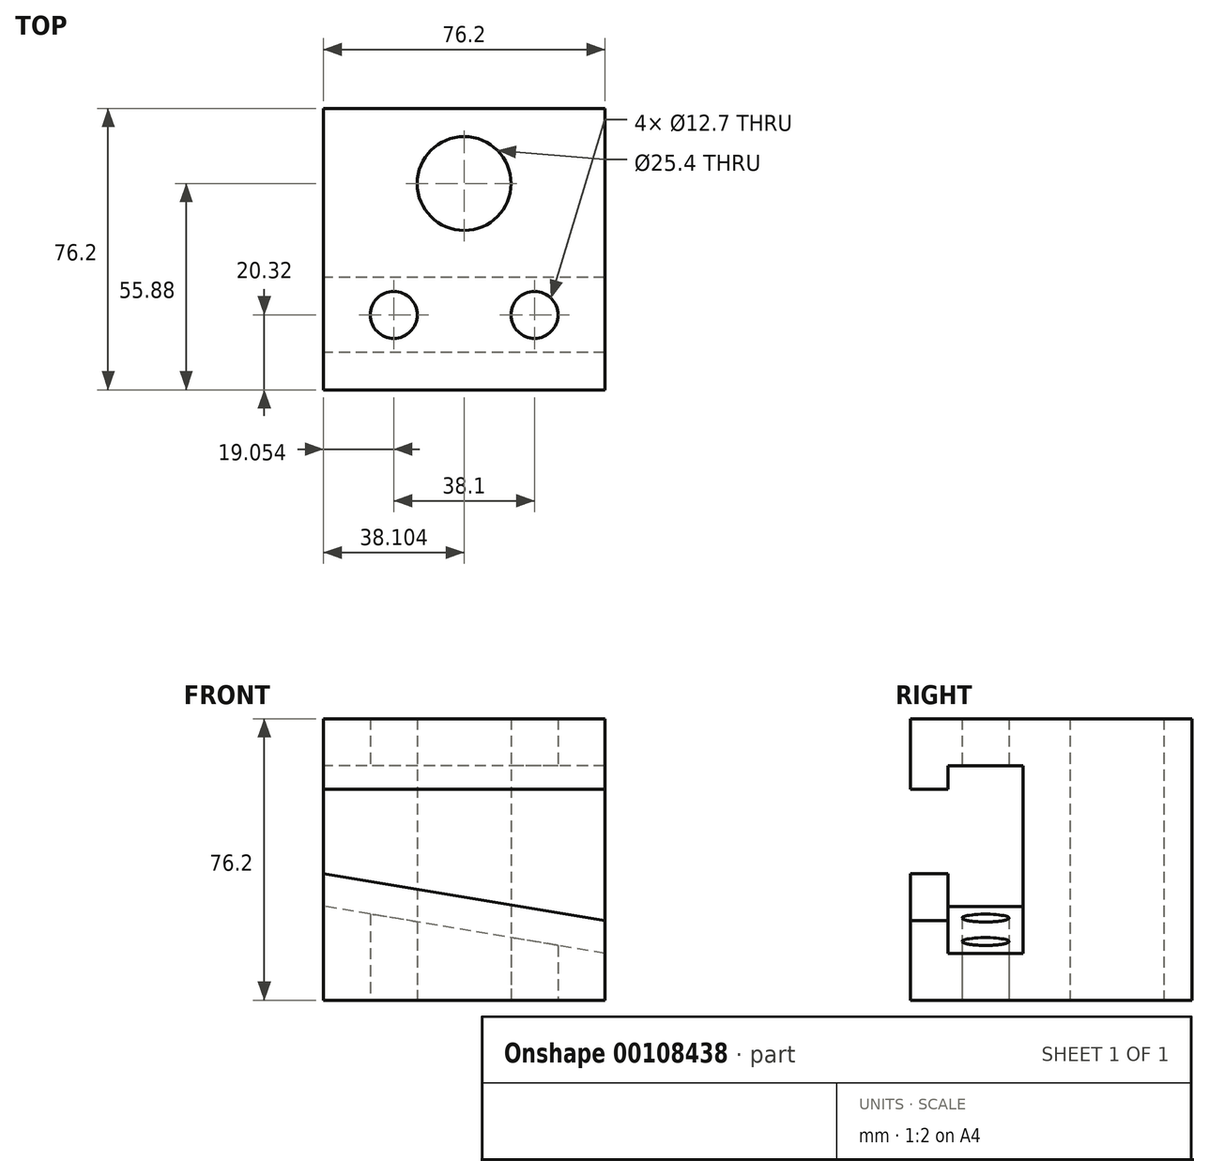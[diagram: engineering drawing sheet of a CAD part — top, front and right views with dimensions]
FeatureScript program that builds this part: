
annotation { "Feature Type Name" : "Feature", "Feature Type Description" : "" }
export const myFeature = defineFeature(function(context is Context, id is Id, definition is map)
    precondition{}
    {
        {
            var Q0;
            Q0=qCreatedBy(makeId("Top.planeOp"),FACE);
            var sketch = newSketch(context, id + "F0", { "sketchPlane" : qUnion([Q0])});
            skLineSegment(sketch, "E0.bottom", {"start": v(-37.22, 43.53) * mm, "end": v(38.98, 43.53) * mm});
            skLineSegment(sketch, "E0.top", {"start": v(-37.22, -32.67) * mm, "end": v(38.98, -32.67) * mm});
            skLineSegment(sketch, "E0.left", {"start": v(-37.22, 43.53) * mm, "end": v(-37.22, -32.67) * mm});
            skLineSegment(sketch, "E0.right", {"start": v(38.98, 43.53) * mm, "end": v(38.98, -32.67) * mm});
            skCircle(sketch, "E1", {"center": v(0.88, 23.21) * mm, "radius": 12.7 * mm});
            skCircle(sketch, "E2", {"center": v(-18.17, -12.35) * mm, "radius": 6.35 * mm});
            skCircle(sketch, "E3", {"center": v(19.93, -12.35) * mm, "radius": 6.35 * mm});
            skSolve(sketch);
        }
        {
            var Q0;
            Q0 = qSketchRegion(id + "F0", true);
            extrude(context, id + "F1", {"entities" : qUnion([Q0]), "depth" : 76.2 * mm});
        }
        {
            var Q0;
            Q0=makeQuery(id+"F1.opExtrude","SWEPT_FACE",FACE,{"disambiguationData":[OSD([sQuery(id+"F0.wireOp",EDGE,"E0.right")])]});
            var sketch = newSketch(context, id + "F2", { "sketchPlane" : qUnion([Q0])});
            skLineSegment(sketch, "E4", {"start": v(-32.67, 57.15) * mm, "end": v(-22.5, 57.15) * mm});
            skLineSegment(sketch, "E5", {"start": v(-22.5, 57.15) * mm, "end": v(-22.5, 63.5) * mm});
            skLineSegment(sketch, "E6", {"start": v(-22.5, 63.5) * mm, "end": v(-2.19, 63.5) * mm});
            skLineSegment(sketch, "E7", {"start": v(-2.19, 63.5) * mm, "end": v(-2.19, 12.7) * mm});
            skLineSegment(sketch, "E8", {"start": v(-2.19, 12.7) * mm, "end": v(-22.5, 12.7) * mm});
            skLineSegment(sketch, "E9", {"start": v(-22.5, 12.7) * mm, "end": v(-22.5, 21.59) * mm});
            skLineSegment(sketch, "E10", {"start": v(-22.5, 21.59) * mm, "end": v(-32.67, 21.59) * mm});
            skLineSegment(sketch, "E11", {"start": v(-32.67, 57.15) * mm, "end": v(-32.67, 21.59) * mm});
            skSolve(sketch);
        }
        {
            var Q0;
            Q0=makeQuery(id+"F1.opExtrude","SWEPT_FACE",FACE,{"disambiguationData":[OSD([sQuery(id+"F0.wireOp",EDGE,"E0.left")])]});
            var sketch = newSketch(context, id + "F3", { "sketchPlane" : qUnion([Q0])});
            skLineSegment(sketch, "E12", {"start": v(32.67, 34.3) * mm, "end": v(22.5, 34.3) * mm});
            skLineSegment(sketch, "E13", {"start": v(22.5, 34.3) * mm, "end": v(22.5, 25.4) * mm});
            skLineSegment(sketch, "E14", {"start": v(22.5, 25.4) * mm, "end": v(2.19, 25.4) * mm});
            skLineSegment(sketch, "E15", {"start": v(2.19, 25.4) * mm, "end": v(2.19, 63.5) * mm});
            skLineSegment(sketch, "E16", {"start": v(2.19, 63.5) * mm, "end": v(22.5, 63.5) * mm});
            skLineSegment(sketch, "E17", {"start": v(22.5, 63.5) * mm, "end": v(22.5, 57.15) * mm});
            skLineSegment(sketch, "E18", {"start": v(22.5, 57.15) * mm, "end": v(32.67, 57.15) * mm});
            skLineSegment(sketch, "E19", {"start": v(32.67, 34.3) * mm, "end": v(32.67, 57.15) * mm});
            skSolve(sketch);
        }
        {
            var Q1;
            Q1=makeQuery(id+"F2.imprint","IMPRINT",FACE,{"disambiguationData":[TD([[makeQuery(id+"F2.imprint","IMPRINT",EDGE,{"derivedFrom":sQuery(id+"F2.wireOp",EDGE,"E4")}),-1.0]])]});
            var Q2;
            Q2=makeQuery(id+"F3.imprint","IMPRINT",FACE,{"disambiguationData":[TD([[makeQuery(id+"F3.imprint","IMPRINT",EDGE,{"derivedFrom":sQuery(id+"F3.wireOp",EDGE,"E12")}),-1.0]])]});
            loft(context, id + "F4", {"operationType" : NewBodyOperationType.REMOVE, "sheetProfilesArray" : [{ "sheetProfileEntities" : qUnion([Q1]) }, { "sheetProfileEntities" : qUnion([Q2]) }]});
        }
    });
